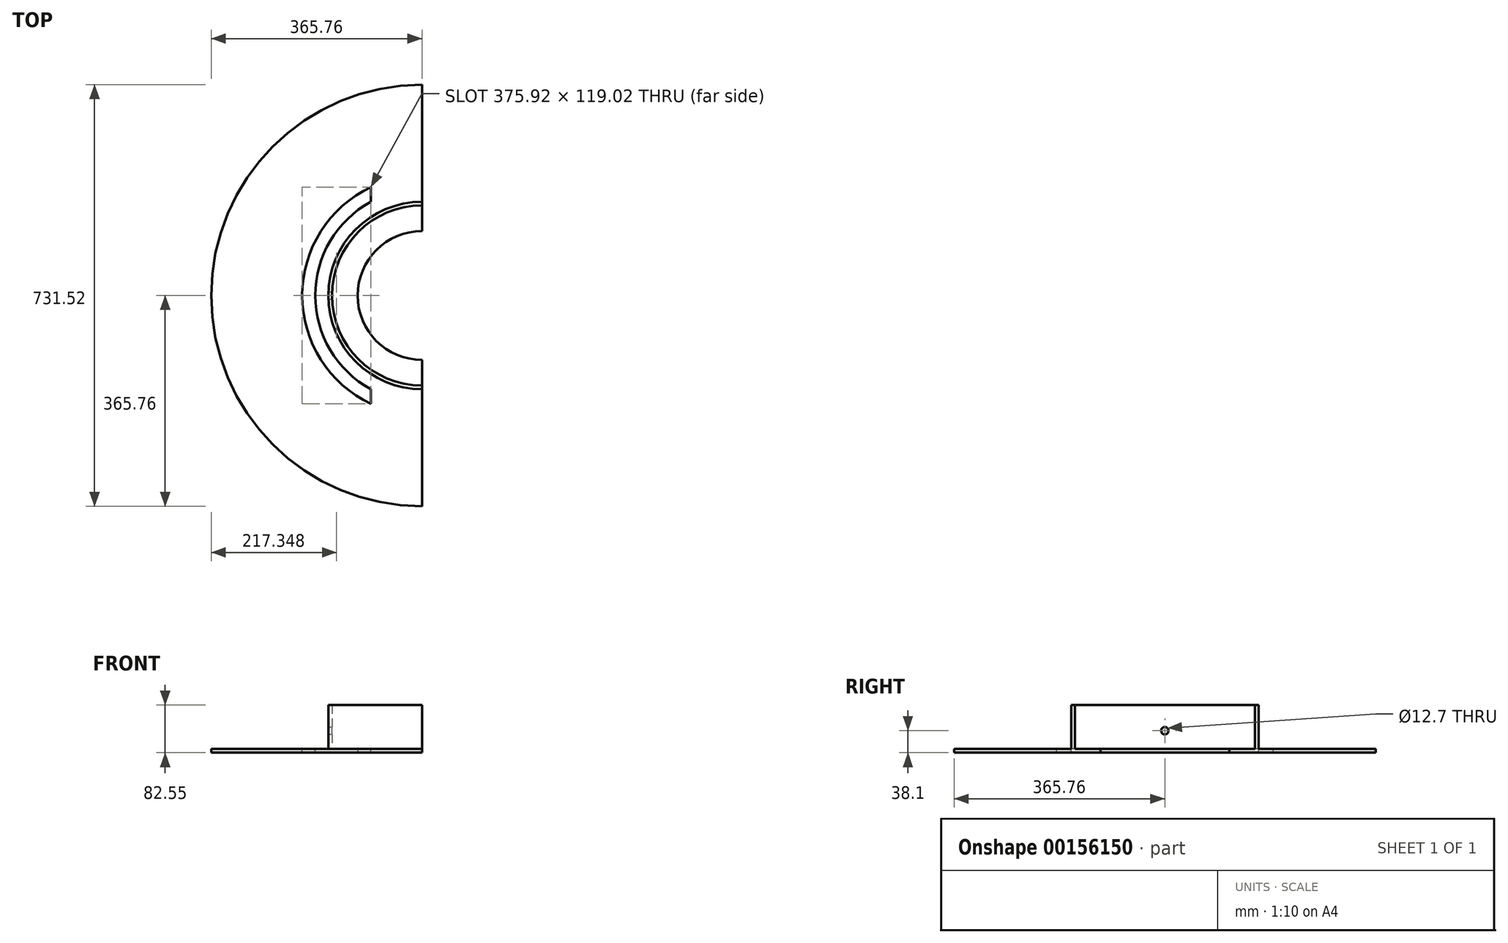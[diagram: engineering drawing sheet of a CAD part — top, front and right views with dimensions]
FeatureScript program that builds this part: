
annotation { "Feature Type Name" : "Feature", "Feature Type Description" : "" }
export const myFeature = defineFeature(function(context is Context, id is Id, definition is map)
    precondition{}
    {
        {
            var Q0;
            Q0=qCreatedBy(makeId("Top.planeOp"),FACE);
            var sketch = newSketch(context, id + "F0", { "sketchPlane" : qUnion([Q0])});
            skCircle(sketch, "E0", {"center": v(0, 0) * mm, "radius": 111.76 * mm});
            skCircle(sketch, "E1", {"center": v(0, 0) * mm, "radius": 365.76 * mm});
            skSolve(sketch);
        }
        {
            var Q0;
            Q0=makeQuery(id+"F0.imprint","IMPRINT",FACE,{"disambiguationData":[TD([[makeQuery(id+"F0.imprint","IMPRINT",EDGE,{"derivedFrom":sQuery(id+"F0.wireOp",EDGE,"E0")}),-1.0]])]});
            extrude(context, id + "F1", {"entities" : qUnion([Q0]), "depth" : 6.35 * mm});
        }
        {
            var Q0;
            Q0=makeQuery(id+"F1.opExtrude","CAP_FACE",FACE,{"disambiguationData":[OSD([sQuery(id+"F0.wireOp",EDGE,"E0"),sQuery(id+"F0.wireOp",EDGE,"E1")])],"isStart":false});
            var sketch = newSketch(context, id + "F2", { "sketchPlane" : qUnion([Q0])});
            skLineSegment(sketch, "E2.bottom", {"start": v(0, 394.93) * mm, "end": v(380.01, 394.93) * mm});
            skLineSegment(sketch, "E2.top", {"start": v(0, -392.69) * mm, "end": v(380.01, -392.69) * mm});
            skLineSegment(sketch, "E2.left", {"start": v(0, 394.93) * mm, "end": v(0, -392.69) * mm});
            skLineSegment(sketch, "E2.right", {"start": v(380.01, 394.93) * mm, "end": v(380.01, -392.69) * mm});
            skSolve(sketch);
        }
        {
            var Q0;
            Q0=qSketchRegion(id+"F2",true);
            extrude(context, id + "F3", {"entities" : qUnion([Q0]), "operationType" : NewBodyOperationType.REMOVE, "endBound" : BoundingType.THROUGH_ALL, "oppositeDirection" : true, "depth" : 25.4 * mm});
        }
        {
            var Q0;
            Q0=makeQuery(id+"F1.opExtrude","CAP_FACE",FACE,{"disambiguationData":[OSD([sQuery(id+"F0.wireOp",EDGE,"E0"),sQuery(id+"F0.wireOp",EDGE,"E1")])],"isStart":false});
            var sketch = newSketch(context, id + "F4", { "sketchPlane" : qUnion([Q0])});
            skLineSegment(sketch, "E3.right", {"start": v(-88.9, -289.56) * mm, "end": v(-88.9, -264.16) * mm});
            skLineSegment(sketch, "E4.right", {"start": v(-88.9, 264.16) * mm, "end": v(-88.9, 289.56) * mm});
            skPoint(sketch, "E5.middle.positionSnap0", {"position": v(-365.76, 0) * mm});
            skPoint(sketch, "E5.centerSnap0", {"position": v(-365.76, 0) * mm});
            skLineSegment(sketch, "E6.left", {"start": v(-88.9, -162.56) * mm, "end": v(-88.9, -187.96) * mm});
            skLineSegment(sketch, "E7.left", {"start": v(-88.9, 187.96) * mm, "end": v(-88.9, 162.56) * mm});
            skCircle(sketch, "E8", {"center": v(0, 0) * mm, "radius": 302.9 * mm});
            skCircle(sketch, "E9", {"center": v(0, 0) * mm, "radius": 278.72 * mm});
            skCircle(sketch, "E10", {"center": v(0, 0) * mm, "radius": 207.92 * mm});
            skCircle(sketch, "E11", {"center": v(0, 0) * mm, "radius": 185.28 * mm});
            skLineSegment(sketch, "E12", {"start": v(-88.9, 289.56) * mm, "end": v(-88.9, 264.16) * mm});
            skLineSegment(sketch, "E13", {"start": v(-88.9, -264.16) * mm, "end": v(-88.9, -289.56) * mm});
            skSolve(sketch);
        }
        {
            var Q0;
            {var subQ0=sQuery(id+"F4.wireOp",EDGE,"E12");Q0=makeQuery(id+"F4.imprint","IMPRINT",FACE,{"disambiguationData":[TD([[makeQuery(id+"F4.imprint","IMPRINT",EDGE,{"derivedFrom":subQ0}),-1.0]])]});}
            var Q1;
            {var subQ0=sQuery(id+"F4.wireOp",EDGE,"E7.left");Q1=makeQuery(id+"F4.imprint","IMPRINT",FACE,{"disambiguationData":[TD([[makeQuery(id+"F4.imprint","IMPRINT",EDGE,{"derivedFrom":subQ0}),-1.0]])]});}
            extrude(context, id + "F5", {"entities" : qUnion([Q0, Q1]), "operationType" : NewBodyOperationType.REMOVE, "endBound" : BoundingType.THROUGH_ALL, "oppositeDirection" : true, "depth" : 25.4 * mm});
        }
        {
            var Q0;
            Q0=makeQuery(id+"F1.opExtrude","CAP_FACE",FACE,{"disambiguationData":[OSD([sQuery(id+"F0.wireOp",EDGE,"E0"),sQuery(id+"F0.wireOp",EDGE,"E1")])],"isStart":false});
            var sketch = newSketch(context, id + "F6", { "sketchPlane" : qUnion([Q0])});
            skArc(sketch, "E14.0", {"start": v(0, 162.56) * mm, "mid": v(-162.56, 0) * mm, "end": v(0, -162.56) * mm});
            skArc(sketch, "E15.0", {"start": v(0, 156.21) * mm, "mid": v(-156.21, 0) * mm, "end": v(0, -156.21) * mm});
            skLineSegment(sketch, "E16", {"start": v(0, 162.56) * mm, "end": v(0, 156.21) * mm});
            skLineSegment(sketch, "E17", {"start": v(0, -156.21) * mm, "end": v(0, -162.56) * mm});
            skSolve(sketch);
        }
        {
            var Q0;
            Q0=qSketchRegion(id+"F6",true);
            extrude(context, id + "F7", {"entities" : qUnion([Q0]), "operationType" : NewBodyOperationType.ADD, "depth" : 76.2 * mm, "offsetDistance" : 25.4 * mm});
        }
        {
            var Q0;
            Q0=qCreatedBy(makeId("Right.planeOp"),FACE);
            var sketch = newSketch(context, id + "F8", { "sketchPlane" : qUnion([Q0])});
            skCircle(sketch, "E18", {"center": v(0, 38.1) * mm, "radius": 6.35 * mm});
            skSolve(sketch);
        }
        {
            var Q0;
            Q0=qSketchRegion(id+"F8",true);
            extrude(context, id + "F9", {"entities" : qUnion([Q0]), "operationType" : NewBodyOperationType.REMOVE, "endBound" : BoundingType.THROUGH_ALL, "oppositeDirection" : true, "depth" : 25.4 * mm, "offsetDistance" : 25.4 * mm});
        }
    });
